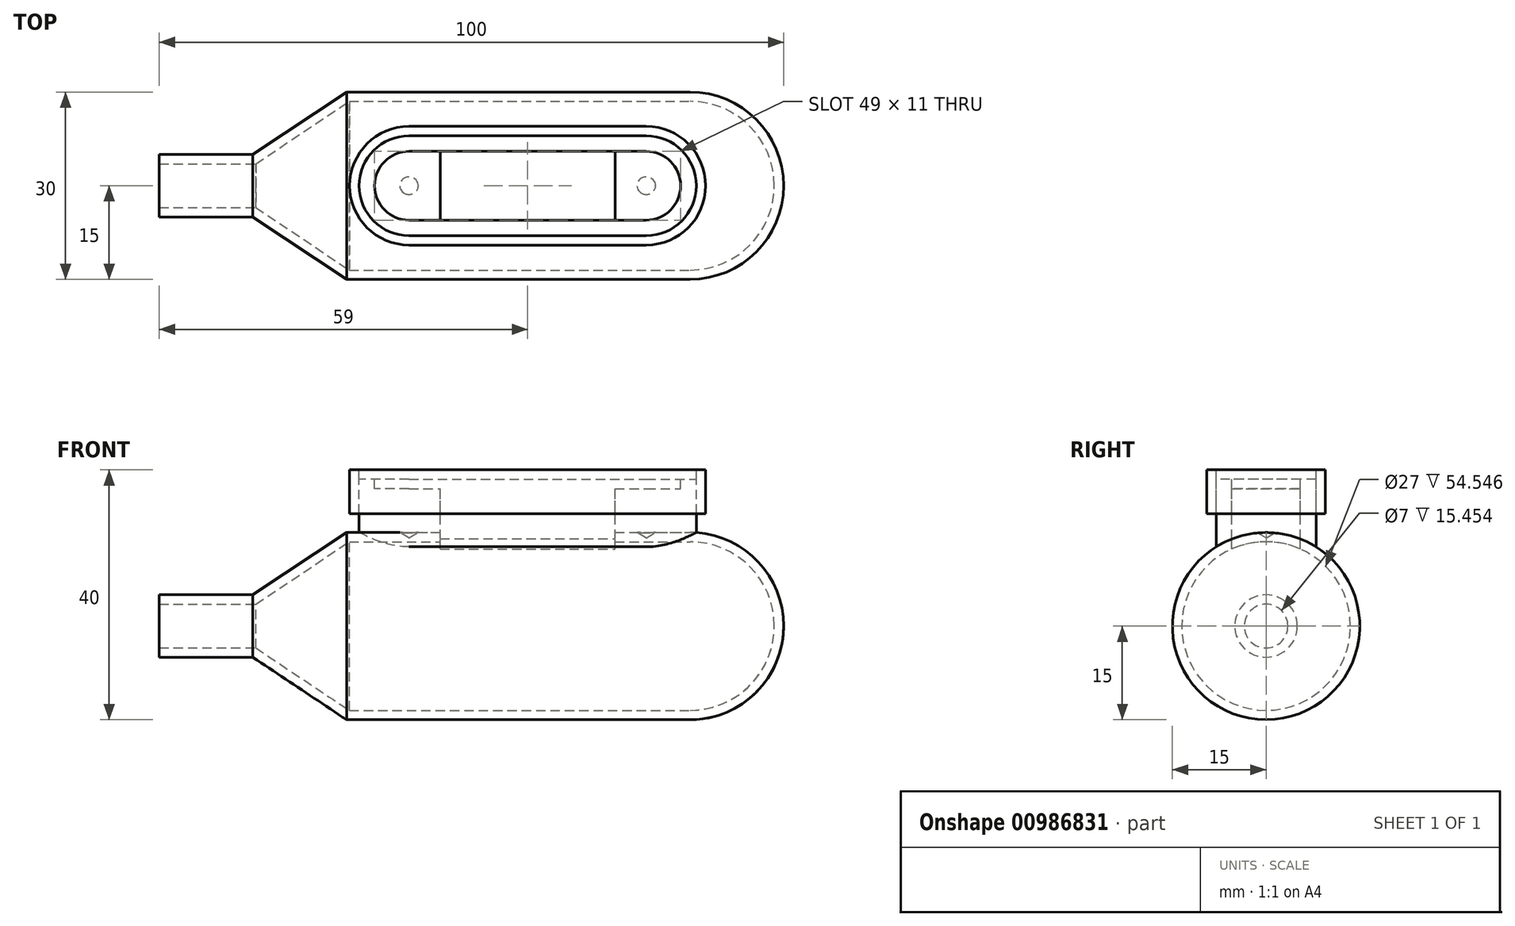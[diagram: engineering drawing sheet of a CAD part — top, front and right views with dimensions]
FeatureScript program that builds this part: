
annotation { "Feature Type Name" : "Feature", "Feature Type Description" : "" }
export const myFeature = defineFeature(function(context is Context, id is Id, definition is map)
    precondition{}
    {
        {
            var Q0;
            Q0=qCreatedBy(makeId("Front.planeOp"),FACE);
            var sketch = newSketch(context, id + "F0", { "sketchPlane" : qUnion([Q0])});
            skLineSegment(sketch, "E0", {"start": v(0, 0) * mm, "end": v(0, 5) * mm});
            skLineSegment(sketch, "E1", {"start": v(0, 5) * mm, "end": v(15, 5) * mm});
            skLineSegment(sketch, "E2", {"start": v(15, 5) * mm, "end": v(30, 15) * mm});
            skLineSegment(sketch, "E3", {"start": v(30, 15) * mm, "end": v(85, 15) * mm});
            skLineSegment(sketch, "E4", {"start": v(100, 0) * mm, "end": v(0, 0) * mm});
            skArc(sketch, "E5.filletArc", {"start": v(100, 0) * mm, "mid": v(95.6, 10.6) * mm, "end": v(85, 15) * mm});
            skSolve(sketch);
        }
        {
            var Q0;
            Q0=makeQuery(id+"F0.imprint","IMPRINT",FACE,{"disambiguationData":[TD([[makeQuery(id+"F0.imprint","IMPRINT",EDGE,{"derivedFrom":sQuery(id+"F0.wireOp",EDGE,"E0")}),-1.0]])]});
            var Q1;
            Q1=sQuery(id+"F0.wireOp",EDGE,"E4");
            revolve(context, id + "F1", {"surfaceOperationType" : NewSurfaceOperationType.NEW, "entities" : qUnion([Q0]), "axis" : qUnion([Q1]), "revolveType" : RevolveType.FULL});
        }
        {
            var Q0;
            Q0=makeQuery(id+"F1.opRevolve","SWEPT_FACE",FACE,{"disambiguationData":[OSD([sQuery(id+"F0.wireOp",EDGE,"E0")])]});
            shell(context, id + "F2", {"entities" : qUnion([Q0]), "thickness" : 1.5 * mm});
        }
        {
            var Q0;
            Q0=qCreatedBy(makeId("Top.planeOp"),FACE);
            cPlane(context, id + "F3", {"entities" : qUnion([Q0]), "cplaneType" : CPlaneType.OFFSET, "offset" : 25 * mm, "width" : 150 * mm, "height" : 150 * mm});
        }
        {
            var Q0;
            Q0=qCreatedBy(id+"F3.planeOp",FACE);
            var sketch = newSketch(context, id + "F4", { "sketchPlane" : qUnion([Q0])});
            skLineSegment(sketch, "E6.bottom", {"start": v(30.5, 9.5) * mm, "end": v(87.5, 9.5) * mm});
            skLineSegment(sketch, "E6.top", {"start": v(30.5, -9.5) * mm, "end": v(87.5, -9.5) * mm});
            skLineSegment(sketch, "E6.left", {"start": v(30.5, 9.5) * mm, "end": v(30.5, -9.5) * mm});
            skLineSegment(sketch, "E6.right", {"start": v(87.5, 9.5) * mm, "end": v(87.5, -9.5) * mm});
            skSolve(sketch);
        }
        {
            var Q0;
            Q0=makeQuery(id+"F4.imprint","IMPRINT",FACE,{"disambiguationData":[TD([[makeQuery(id+"F4.imprint","IMPRINT",EDGE,{"derivedFrom":sQuery(id+"F4.wireOp",EDGE,"E6.bottom")}),-1.0]])]});
            extrude(context, id + "F5", {"entities" : qUnion([Q0]), "oppositeDirection" : true, "depth" : 7 * mm, "offsetDistance" : 25 * mm});
        }
        {
            var Q0;
            Q0=makeQuery(id+"F5.opExtrude","SWEPT_EDGE",EDGE,{"disambiguationData":[OSD([sQuery(id+"F4.wireOp",EDGE,"E6.top"),sQuery(id+"F4.wireOp",EDGE,"E6.left")])]});
            var Q1;
            Q1=makeQuery(id+"F5.opExtrude","SWEPT_EDGE",EDGE,{"disambiguationData":[OSD([sQuery(id+"F4.wireOp",EDGE,"E6.top"),sQuery(id+"F4.wireOp",EDGE,"E6.right")])]});
            var Q2;
            Q2=makeQuery(id+"F5.opExtrude","SWEPT_EDGE",EDGE,{"disambiguationData":[OSD([sQuery(id+"F4.wireOp",EDGE,"E6.bottom"),sQuery(id+"F4.wireOp",EDGE,"E6.left")])]});
            var Q3;
            Q3=makeQuery(id+"F5.opExtrude","SWEPT_EDGE",EDGE,{"disambiguationData":[OSD([sQuery(id+"F4.wireOp",EDGE,"E6.bottom"),sQuery(id+"F4.wireOp",EDGE,"E6.right")])]});
            fillet(context, id + "F6", {"entities" : qUnion([Q0, Q1, Q2, Q3]), "radius" : 9.5 * mm, "tangentPropagation" : true, "allowEdgeOverflow" : false});
        }
        {
            var Q0;
            Q0=qCreatedBy(id+"F3.planeOp",FACE);
            var sketch = newSketch(context, id + "F7", { "sketchPlane" : qUnion([Q0])});
            skLineSegment(sketch, "E7.bottom", {"start": v(40, 8) * mm, "end": v(78, 8) * mm});
            skLineSegment(sketch, "E7.top", {"start": v(40, -8) * mm, "end": v(78, -8) * mm});
            skLineSegment(sketch, "E7.left", {"start": v(32, 0) * mm, "end": v(32, 0) * mm});
            skLineSegment(sketch, "E7.right", {"start": v(86, 0) * mm, "end": v(86, 0) * mm});
            skPoint(sketch, "E8.visualSharp", {"position": v(32, 8) * mm});
            skArc(sketch, "E8.filletArc", {"start": v(40, 8) * mm, "mid": v(34.34, 5.66) * mm, "end": v(32, 0) * mm});
            skPoint(sketch, "E9.visualSharp", {"position": v(32, -8) * mm});
            skArc(sketch, "E9.filletArc", {"start": v(32, 0) * mm, "mid": v(34.34, -5.66) * mm, "end": v(40, -8) * mm});
            skPoint(sketch, "E10.visualSharp", {"position": v(86, -8) * mm});
            skArc(sketch, "E10.filletArc", {"start": v(78, -8) * mm, "mid": v(83.66, -5.66) * mm, "end": v(86, 0) * mm});
            skPoint(sketch, "E11.visualSharp", {"position": v(86, 8) * mm});
            skArc(sketch, "E11.filletArc", {"start": v(86, 0) * mm, "mid": v(83.66, 5.66) * mm, "end": v(78, 8) * mm});
            skSolve(sketch);
        }
        {
            var Q0;
            Q0 = qSketchRegion(id + "F7", true);
            var Q1;
            Q1=makeQuery(id+"F1.opRevolve","SWEPT_BODY",BODY,{"disambiguationData":[OSD([sQuery(id+"F0.wireOp",EDGE,"E0"),sQuery(id+"F0.wireOp",EDGE,"E1"),sQuery(id+"F0.wireOp",EDGE,"E2"),sQuery(id+"F0.wireOp",EDGE,"E3"),sQuery(id+"F0.wireOp",EDGE,"E4"),sQuery(id+"F0.wireOp",EDGE,"E5.filletArc")])]});
            extrude(context, id + "F8", {"entities" : qUnion([Q0]), "endBound" : BoundingType.UP_TO_BODY, "oppositeDirection" : true, "depth" : 25 * mm, "endBoundEntityBody" : qUnion([Q1]), "offsetDistance" : 25 * mm});
        }
        {
            var Q0;
            Q0=qCreatedBy(id+"F3.planeOp",FACE);
            var sketch = newSketch(context, id + "F9", { "sketchPlane" : qUnion([Q0])});
            skArc(sketch, "E12.0", {"start": v(40, 8) * mm, "mid": v(34.34, 5.66) * mm, "end": v(32, 0) * mm});
            skLineSegment(sketch, "E13.0", {"start": v(40, 8) * mm, "end": v(78, 8) * mm});
            skArc(sketch, "E14.0", {"start": v(86, 0) * mm, "mid": v(83.66, 5.66) * mm, "end": v(78, 8) * mm});
            skArc(sketch, "E15.0", {"start": v(78, -8) * mm, "mid": v(83.66, -5.66) * mm, "end": v(86, 0) * mm});
            skLineSegment(sketch, "E16.0", {"start": v(40, -8) * mm, "end": v(78, -8) * mm});
            skArc(sketch, "E17.0", {"start": v(32, 0) * mm, "mid": v(34.34, -5.66) * mm, "end": v(40, -8) * mm});
            skSolve(sketch);
        }
        {
            var Q0;
            Q0 = qSketchRegion(id + "F9", true);
            extrude(context, id + "F10", {"entities" : qUnion([Q0]), "operationType" : NewBodyOperationType.REMOVE, "oppositeDirection" : true, "depth" : 1.5 * mm, "offsetDistance" : 25 * mm});
        }
        {
            var Q0;
            Q0=qCreatedBy(id+"F3.planeOp",FACE);
            var sketch = newSketch(context, id + "F11", { "sketchPlane" : qUnion([Q0])});
            skArc(sketch, "E18.0", {"start": v(40, 5.5) * mm, "mid": v(36.11, 3.89) * mm, "end": v(34.5, 0) * mm});
            skArc(sketch, "E18.1", {"start": v(83.5, 0) * mm, "mid": v(81.89, 3.89) * mm, "end": v(78, 5.5) * mm});
            skArc(sketch, "E18.2", {"start": v(78, -5.5) * mm, "mid": v(81.89, -3.89) * mm, "end": v(83.5, 0) * mm});
            skLineSegment(sketch, "E18.3", {"start": v(40, 5.5) * mm, "end": v(78, 5.5) * mm});
            skLineSegment(sketch, "E18.4", {"start": v(40, -5.5) * mm, "end": v(78, -5.5) * mm});
            skArc(sketch, "E18.5", {"start": v(34.5, 0) * mm, "mid": v(36.11, -3.89) * mm, "end": v(40, -5.5) * mm});
            skSolve(sketch);
        }
        {
            var Q0;
            Q0=makeQuery(id+"F11.imprint","IMPRINT",FACE,{"disambiguationData":[TD([[makeQuery(id+"F11.imprint","IMPRINT",EDGE,{"derivedFrom":sQuery(id+"F11.wireOp",EDGE,"E18.0")}),1.0]])]});
            extrude(context, id + "F12", {"entities" : qUnion([Q0]), "operationType" : NewBodyOperationType.REMOVE, "oppositeDirection" : true, "depth" : 3 * mm, "offsetDistance" : 25 * mm});
        }
        {
            var Q0;
            Q0=qCreatedBy(id+"F3.planeOp",FACE);
            var sketch = newSketch(context, id + "F13", { "sketchPlane" : qUnion([Q0])});
            skLineSegment(sketch, "E19.bottom", {"start": v(45, 5.5) * mm, "end": v(73, 5.5) * mm});
            skLineSegment(sketch, "E19.top", {"start": v(45, -5.5) * mm, "end": v(73, -5.5) * mm});
            skLineSegment(sketch, "E19.left", {"start": v(45, 5.5) * mm, "end": v(45, -5.5) * mm});
            skLineSegment(sketch, "E19.right", {"start": v(73, 5.5) * mm, "end": v(73, -5.5) * mm});
            skLineSegment(sketch, "E20", {"start": v(59, 5.5) * mm, "end": v(59, -5.5) * mm, "construction": true});
            skSolve(sketch);
        }
        {
            var Q0;
            Q0=makeQuery(id+"F13.imprint","IMPRINT",FACE,{"disambiguationData":[TD([[makeQuery(id+"F13.imprint","IMPRINT",EDGE,{"derivedFrom":sQuery(id+"F13.wireOp",EDGE,"E19.bottom")}),-1.0]])]});
            var Q1;
            Q1=qCreatedBy(makeId("Top.planeOp"),FACE);
            extrude(context, id + "F14", {"entities" : qUnion([Q0]), "operationType" : NewBodyOperationType.REMOVE, "endBound" : BoundingType.UP_TO_SURFACE, "oppositeDirection" : true, "depth" : 25 * mm, "endBoundEntityFace" : qUnion([Q1]), "offsetDistance" : 25 * mm});
        }
        {
            var Q0;
            Q0=sQuery(id+"F7.wireOp",VERTEX,"E8.filletArc.center");
            var Q1;
            Q1=sQuery(id+"F7.wireOp",VERTEX,"E10.filletArc.center");
            var Q2;
            Q2=makeQuery(id+"F1.opRevolve","SWEPT_BODY",BODY,{"disambiguationData":[OSD([sQuery(id+"F0.wireOp",EDGE,"E0"),sQuery(id+"F0.wireOp",EDGE,"E1"),sQuery(id+"F0.wireOp",EDGE,"E2"),sQuery(id+"F0.wireOp",EDGE,"E3"),sQuery(id+"F0.wireOp",EDGE,"E4"),sQuery(id+"F0.wireOp",EDGE,"E5.filletArc")])]});
            hole(context, id + "F15", {"style" : HoleStyle.SIMPLE, "endStyle" : HoleEndStyle.BLIND, "holeDiameter" : 3 * mm, "majorDiameter" : 5 * mm, "holeDepth" : 10 * mm, "isTappedThrough" : true, "tappedDepth" : 12 * mm, "tapClearance" : 3, "startFromSketch" : true, "locations" : qUnion([Q0, Q1]), "scope" : qUnion([Q2])});
        }
    });
